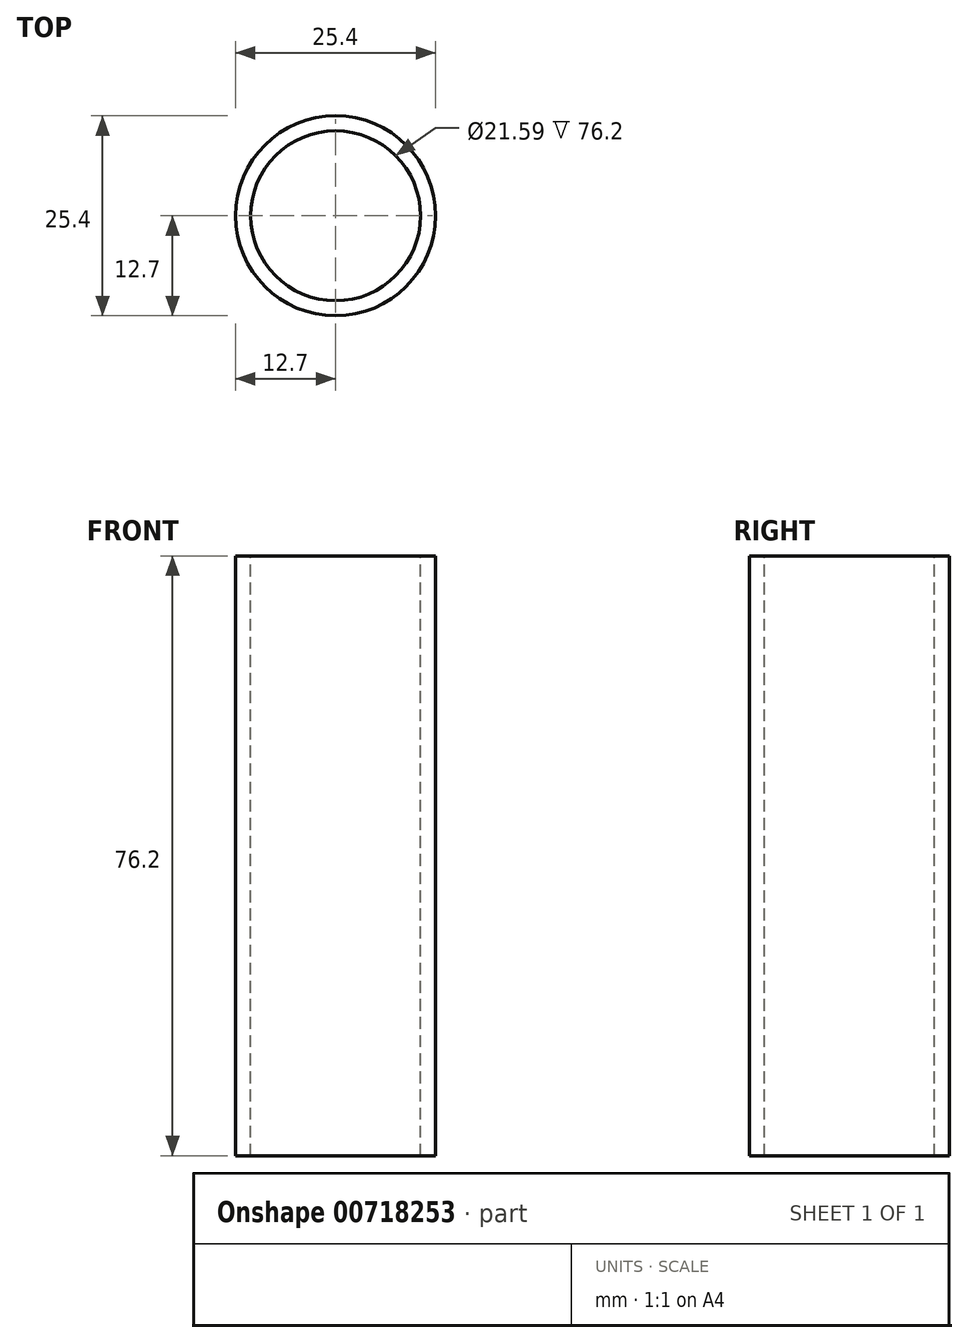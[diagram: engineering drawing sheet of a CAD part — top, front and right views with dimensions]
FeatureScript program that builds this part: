
annotation { "Feature Type Name" : "Feature", "Feature Type Description" : "" }
export const myFeature = defineFeature(function(context is Context, id is Id, definition is map)
    precondition{}
    {
        {
            var Q0;
            Q0=qCreatedBy(makeId("Top.planeOp"),FACE);
            var sketch = newSketch(context, id + "F0", { "sketchPlane" : qUnion([Q0])});
            skCircle(sketch, "E0", {"center": v(0, 0) * mm, "radius": 12.7 * mm});
            skSolve(sketch);
        }
        {
            var Q0;
            Q0 = qSketchRegion(id + "F0", true);
            extrude(context, id + "F1", {"entities" : qUnion([Q0]), "depth" : 50.8 * mm, "offsetDistance" : 25.4 * mm});
        }
        {
            var Q0;
            Q0=makeQuery(id+"F1.opExtrude","CAP_FACE",FACE,{"disambiguationData":[OSD([sQuery(id+"F0.wireOp",EDGE,"E0")])],"isStart":false});
            extrude(context, id + "F2", {"entities" : qUnion([Q0]), "operationType" : NewBodyOperationType.ADD, "depth" : 25.4 * mm, "offsetDistance" : 25.4 * mm});
        }
        {
            var Q0;
            Q0=makeQuery(id+"F2.opExtrude","CAP_FACE",FACE,{"disambiguationData":[OSD([sQuery(id+"F0.wireOp",EDGE,"E0")])],"isStart":false});
            var sketch = newSketch(context, id + "F3", { "sketchPlane" : qUnion([Q0])});
            skCircle(sketch, "E1", {"center": v(0, 0) * mm, "radius": 9.2 * mm});
            skSolve(sketch);
        }
        {
            var Q0;
            Q0=sQuery(id+"F3.wireOp",VERTEX,"E1.center");
            var Q1;
            Q1=makeQuery(id+"F1.opExtrude","SWEPT_BODY",BODY,{"disambiguationData":[OSD([sQuery(id+"F0.wireOp",EDGE,"E0")])]});
            hole(context, id + "F4", {"style" : HoleStyle.SIMPLE, "endStyle" : HoleEndStyle.THROUGH, "holeDiameter" : 21.59 * mm, "majorDiameter" : 6.35 * mm, "isTappedThrough" : true, "tappedDepth" : 12.7 * mm, "tapClearance" : 3, "locations" : qUnion([Q0]), "scope" : qUnion([Q1])});
        }
    });
